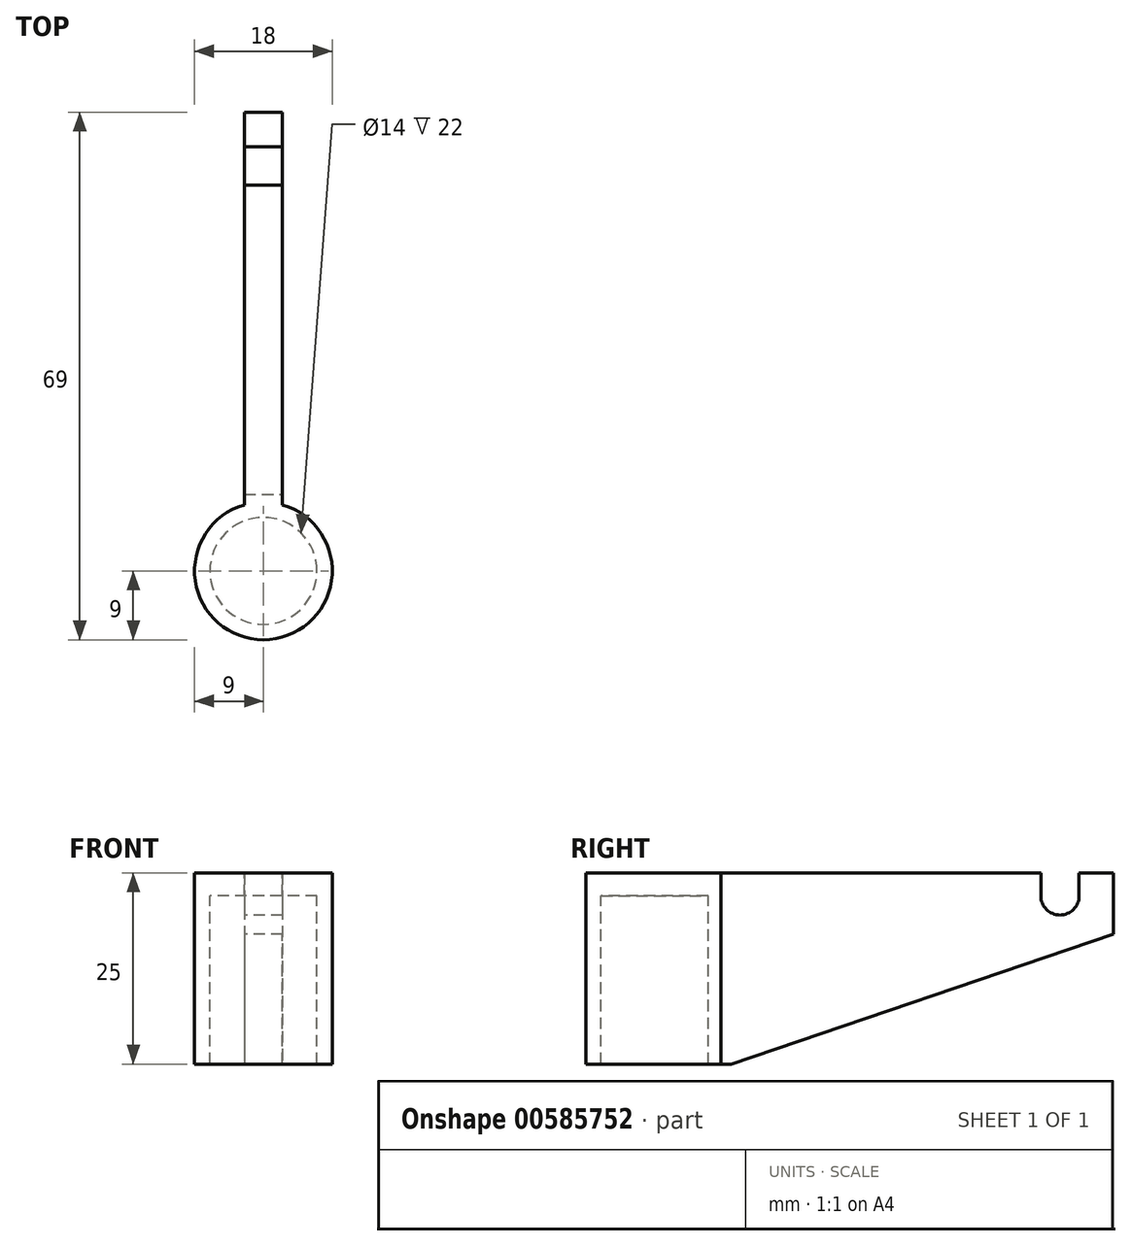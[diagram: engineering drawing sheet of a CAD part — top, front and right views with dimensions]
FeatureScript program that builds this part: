
annotation { "Feature Type Name" : "Feature", "Feature Type Description" : "" }
export const myFeature = defineFeature(function(context is Context, id is Id, definition is map)
    precondition{}
    {
        {
            var Q0;
            Q0=qCreatedBy(makeId("Top.planeOp"),FACE);
            var sketch = newSketch(context, id + "F0", { "sketchPlane" : qUnion([Q0])});
            skCircle(sketch, "E0", {"center": v(0, 0) * mm, "radius": 7 * mm});
            skCircle(sketch, "E1", {"center": v(0, 0) * mm, "radius": 9 * mm});
            skLineSegment(sketch, "E2.bottom", {"start": v(-2.5, 8.65) * mm, "end": v(2.5, 8.65) * mm});
            skLineSegment(sketch, "E2.top", {"start": v(-2.5, 60) * mm, "end": v(2.5, 60) * mm});
            skLineSegment(sketch, "E2.left", {"start": v(-2.5, 8.65) * mm, "end": v(-2.5, 60) * mm});
            skLineSegment(sketch, "E2.right", {"start": v(2.5, 8.65) * mm, "end": v(2.5, 60) * mm});
            skSolve(sketch);
        }
        {
            var Q0;
            Q0=makeQuery(id+"F0.imprint","IMPRINT",FACE,{"disambiguationData":[TD([[makeQuery(id+"F0.imprint","IMPRINT",EDGE,{"derivedFrom":sQuery(id+"F0.wireOp",EDGE,"E0")}),-1.0]])]});
            var Q1;
            Q1=makeQuery(id+"F0.imprint","IMPRINT",FACE,{"disambiguationData":[TD([[makeQuery(id+"F0.imprint","IMPRINT",EDGE,{"derivedFrom":sQuery(id+"F0.wireOp",EDGE,"E0")}),1.0]])]});
            var Q2;
            {var subQ0=sQuery(id+"F0.wireOp",EDGE,"E2.bottom");Q2=makeQuery(id+"F0.imprint","IMPRINT",FACE,{"disambiguationData":[TD([[makeQuery(id+"F0.imprint","IMPRINT",EDGE,{"derivedFrom":subQ0}),1.0]])]});}
            var Q3;
            Q3=makeQuery(id+"F0.imprint","IMPRINT",FACE,{"disambiguationData":[TD([[makeQuery(id+"F0.imprint","IMPRINT",EDGE,{"derivedFrom":sQuery(id+"F0.wireOp",EDGE,"E2.top")}),-1.0]])]});
            extrude(context, id + "F1", {"entities" : qUnion([Q0, Q1, Q2, Q3]), "depth" : 3 * mm, "offsetDistance" : 25 * mm});
        }
        {
            var Q0;
            Q0=makeQuery(id+"F0.imprint","IMPRINT",FACE,{"disambiguationData":[TD([[makeQuery(id+"F0.imprint","IMPRINT",EDGE,{"derivedFrom":sQuery(id+"F0.wireOp",EDGE,"E0")}),-1.0]])]});
            var Q1;
            Q1=makeQuery(id+"F0.imprint","IMPRINT",FACE,{"disambiguationData":[TD([[makeQuery(id+"F0.imprint","IMPRINT",EDGE,{"derivedFrom":sQuery(id+"F0.wireOp",EDGE,"E2.top")}),-1.0]])]});
            var Q2;
            {var subQ0=sQuery(id+"F0.wireOp",EDGE,"E2.bottom");Q2=makeQuery(id+"F0.imprint","IMPRINT",FACE,{"disambiguationData":[TD([[makeQuery(id+"F0.imprint","IMPRINT",EDGE,{"derivedFrom":subQ0}),1.0]])]});}
            extrude(context, id + "F2", {"entities" : qUnion([Q0, Q1, Q2]), "operationType" : NewBodyOperationType.ADD, "oppositeDirection" : true, "depth" : 22 * mm, "offsetDistance" : 25 * mm});
        }
        {
            var Q0;
            Q0=makeQuery(id+"F2.opExtrude","CAP_EDGE",EDGE,{"disambiguationData":[OSD([sQuery(id+"F0.wireOp",EDGE,"E2.top")])],"isStart":false});
            chamfer(context, id + "F3", {"entities" : qUnion([Q0]), "chamferType" : ChamferType.TWO_OFFSETS, "width1" : 50 * mm, "oppositeDirection" : false, "width2" : 17 * mm, "tangentPropagation" : true});
        }
        {
            var Q0;
            Q0=qCreatedBy(makeId("Right.planeOp"),FACE);
            var sketch = newSketch(context, id + "F4", { "sketchPlane" : qUnion([Q0])});
            skCircle(sketch, "E3", {"center": v(53, 0) * mm, "radius": 2.5 * mm});
            skLineSegment(sketch, "E4", {"start": v(50.5, 0) * mm, "end": v(50.5, 3) * mm});
            skLineSegment(sketch, "E5", {"start": v(55.5, 0) * mm, "end": v(55.5, 3) * mm});
            skLineSegment(sketch, "E6", {"start": v(55.5, 3) * mm, "end": v(50.5, 3) * mm});
            skSolve(sketch);
        }
        {
            var Q0;
            Q0=makeQuery(id+"F4.imprint","IMPRINT",FACE,{"disambiguationData":[TD([[makeQuery(id+"F4.imprint","IMPRINT",EDGE,{"derivedFrom":sQuery(id+"F4.wireOp",EDGE,"E3")}),1.0]])]});
            var Q1;
            {var subQ0=sQuery(id+"F4.wireOp",EDGE,"E4");Q1=makeQuery(id+"F4.imprint","IMPRINT",FACE,{"disambiguationData":[TD([[makeQuery(id+"F4.imprint","IMPRINT",EDGE,{"derivedFrom":subQ0}),-1.0]])]});}
            extrude(context, id + "F5", {"entities" : qUnion([Q0, Q1]), "operationType" : NewBodyOperationType.REMOVE, "depth" : 25 * mm, "offsetDistance" : 25 * mm, "symmetric" : true});
        }
    });
